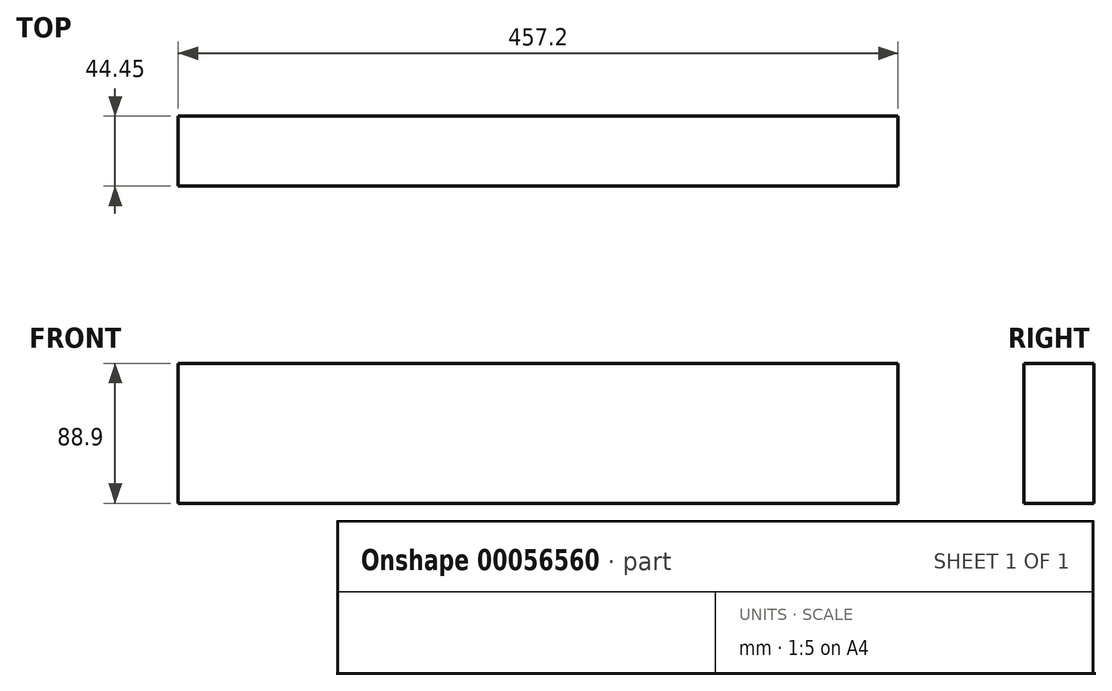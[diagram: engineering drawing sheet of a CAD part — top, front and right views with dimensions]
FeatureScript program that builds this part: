
annotation { "Feature Type Name" : "Feature", "Feature Type Description" : "" }
export const myFeature = defineFeature(function(context is Context, id is Id, definition is map)
    precondition{}
    {
        {
            var Q0;
            Q0=qCreatedBy(makeId("Front.planeOp"),FACE);
            var sketch = newSketch(context, id + "F0", { "sketchPlane" : qUnion([Q0])});
            skLineSegment(sketch, "E0.bottom", {"start": v(0, 0) * mm, "end": v(-457.2, 0) * mm});
            skLineSegment(sketch, "E0.top", {"start": v(0, 88.9) * mm, "end": v(-457.2, 88.9) * mm});
            skLineSegment(sketch, "E0.left", {"start": v(0, 0) * mm, "end": v(0, 88.9) * mm});
            skLineSegment(sketch, "E0.right", {"start": v(-457.2, 0) * mm, "end": v(-457.2, 88.9) * mm});
            skSolve(sketch);
        }
        {
            var Q0;
            Q0=makeQuery(id+"F0.imprint","IMPRINT",FACE,{"disambiguationData":[TD([[makeQuery(id+"F0.imprint","IMPRINT",EDGE,{"derivedFrom":sQuery(id+"F0.wireOp",EDGE,"E0.bottom")}),-1.0]])]});
            extrude(context, id + "F1", {"entities" : qUnion([Q0]), "depth" : 44.45 * mm});
        }
    });
